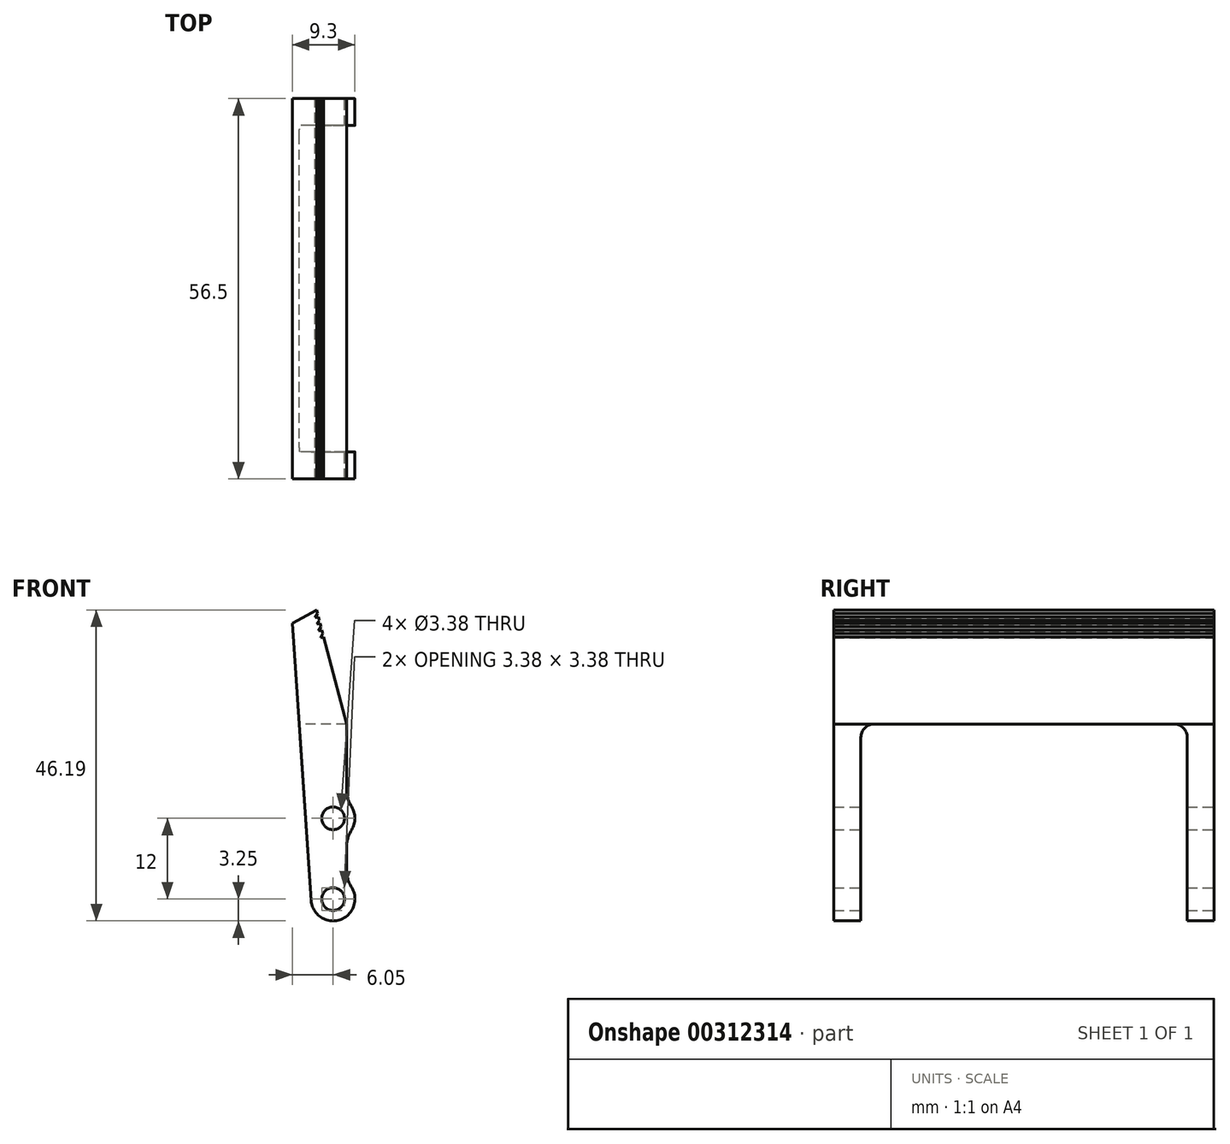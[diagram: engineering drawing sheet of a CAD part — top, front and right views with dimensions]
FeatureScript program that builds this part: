
annotation { "Feature Type Name" : "Feature", "Feature Type Description" : "" }
export const myFeature = defineFeature(function(context is Context, id is Id, definition is map)
    precondition{}
    {
        {
            var Q0;
            Q0=qCreatedBy(makeId("Front.planeOp"),FACE);
            var sketch = newSketch(context, id + "F0", { "sketchPlane" : qUnion([Q0])});
            skCircle(sketch, "E0", {"center": v(0, 0) * mm, "radius": 1.69 * mm});
            skCircle(sketch, "E1", {"center": v(0, 0) * mm, "radius": 2 * mm});
            skLineSegment(sketch, "E2", {"start": v(2, 16) * mm, "end": v(2, 14.56) * mm});
            skLineSegment(sketch, "E3", {"start": v(2, 26.01) * mm, "end": v(2, 16) * mm});
            skLineSegment(sketch, "E4", {"start": v(-6.05, 41) * mm, "end": v(-2, 0) * mm, "construction": true});
            skPoint(sketch, "E5.start.orphan", {"position": v(-6.03, 16) * mm});
            skPoint(sketch, "E6.center.orphan", {"position": v(0, 16) * mm});
            skCircle(sketch, "E7", {"center": v(0, 12) * mm, "radius": 1.69 * mm});
            skLineSegment(sketch, "E8", {"start": v(-6.05, 41) * mm, "end": v(-2.44, 42.94) * mm});
            skLineSegment(sketch, "E9", {"start": v(-2.44, 42.94) * mm, "end": v(2, 26.01) * mm});
            skLineSegment(sketch, "E10", {"start": v(2, 26.01) * mm, "end": v(-6.05, 41) * mm, "construction": true});
            skLineSegment(sketch, "E11", {"start": v(-2.66, 41.81) * mm, "end": v(-2.18, 41.94) * mm});
            skLineSegment(sketch, "E12", {"start": v(-2.31, 42.44) * mm, "end": v(-2.66, 41.81) * mm});
            skLineSegment(sketch, "E13", {"start": v(-2.05, 41.44) * mm, "end": v(-2.4, 40.81) * mm});
            skLineSegment(sketch, "E14", {"start": v(-2.4, 40.81) * mm, "end": v(-1.92, 40.94) * mm});
            skLineSegment(sketch, "E15", {"start": v(-1.79, 40.44) * mm, "end": v(-2.14, 39.81) * mm});
            skLineSegment(sketch, "E16", {"start": v(-2.14, 39.81) * mm, "end": v(-1.66, 39.94) * mm});
            skLineSegment(sketch, "E17", {"start": v(-1.52, 39.44) * mm, "end": v(-1.88, 38.81) * mm});
            skLineSegment(sketch, "E18", {"start": v(-1.88, 38.81) * mm, "end": v(-1.4, 38.94) * mm});
            skCircle(sketch, "E19", {"center": v(0, 0) * mm, "radius": 3.25 * mm});
            skArc(sketch, "E20", {"start": v(2, 9.44) * mm, "mid": v(3.25, 12) * mm, "end": v(2, 14.56) * mm});
            skLineSegment(sketch, "E21.trimOffspring", {"start": v(2, 9.44) * mm, "end": v(2, 0) * mm});
            skLineSegment(sketch, "E22", {"start": v(-3.24, -0.22) * mm, "end": v(-6.05, 41) * mm});
            skSolve(sketch);
        }
        {
            var Q0;
            Q0=makeQuery(id+"F0.imprint","IMPRINT",FACE,{"disambiguationData":[TD([[makeQuery(id+"F0.imprint","IMPRINT",EDGE,{"derivedFrom":sQuery(id+"F0.wireOp",EDGE,"E6")}),-1.0]])]});
            var Q1;
            Q1=makeQuery(id+"F0.imprint","IMPRINT",FACE,{"disambiguationData":[TD([[makeQuery(id+"F0.imprint","IMPRINT",EDGE,{"derivedFrom":sQuery(id+"F0.wireOp",EDGE,"E0")}),-1.0]])]});
            var Q2;
            {var subQ0=sQuery(id+"F0.wireOp",EDGE,"E2");Q2=makeQuery(id+"F0.imprint","IMPRINT",FACE,{"disambiguationData":[TD([[makeQuery(id+"F0.imprint","IMPRINT",EDGE,{"derivedFrom":subQ0}),-1.0]])]});}
            var Q3;
            {var subQ1=sQuery(id+"F0.wireOp",EDGE,"E3");Q3=makeQuery(id+"F0.imprint","IMPRINT",FACE,{"disambiguationData":[TD([[makeQuery(id+"F0.imprint","IMPRINT",EDGE,{"derivedFrom":subQ1}),-1.0]])]});}
            var Q4;
            {var subQ0=sQuery(id+"F0.wireOp",EDGE,"E2");var subQ1=sQuery(id+"F0.wireOp",EDGE,"E1");var subQ2=makeQuery(id+"F0.imprint","INTERSECT",VERTEX,{"derivedFrom":[subQ1,subQ0]});Q4=makeQuery(id+"F0.imprint","IMPRINT",FACE,{"disambiguationData":[TD([[makeQuery(id+"F0.imprint","IMPRINT",EDGE,{"disambiguationData":[TD([[subQ2,1.0]])],"derivedFrom":subQ1}),-1.0]])]});}
            extrude(context, id + "F1", {"entities" : qUnion([Q0, Q1, Q2, Q3, Q4]), "depth" : 56.5 * mm});
        }
        {
            var Q0;
            Q0=makeQuery(id+"F1.opExtrude","CAP_FACE",FACE,{"disambiguationData":[OSD([sQuery(id+"F0.wireOp",EDGE,"E0"),sQuery(id+"F0.wireOp",EDGE,"E1"),sQuery(id+"F0.wireOp",EDGE,"E2"),sQuery(id+"F0.wireOp",EDGE,"E3"),sQuery(id+"F0.wireOp",EDGE,"E4"),sQuery(id+"F0.wireOp",EDGE,"E7"),sQuery(id+"F0.wireOp",EDGE,"E8"),sQuery(id+"F0.wireOp",EDGE,"E9"),sQuery(id+"F0.wireOp",EDGE,"E11"),sQuery(id+"F0.wireOp",EDGE,"E12"),sQuery(id+"F0.wireOp",EDGE,"E13"),sQuery(id+"F0.wireOp",EDGE,"E14"),sQuery(id+"F0.wireOp",EDGE,"E15"),sQuery(id+"F0.wireOp",EDGE,"E16"),sQuery(id+"F0.wireOp",EDGE,"E17"),sQuery(id+"F0.wireOp",EDGE,"E18")])],"isStart":true});
            var sketch = newSketch(context, id + "F2", { "sketchPlane" : qUnion([Q0])});
            skLineSegment(sketch, "E23", {"start": v(-2, 26.01) * mm, "end": v(5.03, 26.01) * mm});
            skLineSegment(sketch, "E24", {"start": v(-2, 26.01) * mm, "end": v(-2.58, 13.98) * mm});
            skArc(sketch, "E25", {"start": v(-2.58, 13.98) * mm, "mid": v(-3.25, 12.16) * mm, "end": v(-2.76, 10.28) * mm});
            skLineSegment(sketch, "E26.trimOffspring", {"start": v(-2.76, 10.28) * mm, "end": v(-3.25, 0.16) * mm});
            skArc(sketch, "E27", {"start": v(-3.25, 0.16) * mm, "mid": v(-0.19, -3.24) * mm, "end": v(3.24, -0.22) * mm});
            skLineSegment(sketch, "E28", {"start": v(5.03, 26.01) * mm, "end": v(3.24, -0.22) * mm});
            skSolve(sketch);
        }
        {
            var Q0;
            Q0 = qSketchRegion(id + "F2", true);
            extrude(context, id + "F3", {"entities" : qUnion([Q0]), "operationType" : NewBodyOperationType.REMOVE, "oppositeDirection" : true, "depth" : 52.5 * mm, "hasSecondDirection" : true, "secondDirectionOppositeDirection" : true, "secondDirectionDepth" : 4 * mm});
        }
        {
            var Q0;
            {var subQ0=sQuery(id+"F0.wireOp",EDGE,"E19");var subQ1=sQuery(id+"F0.wireOp",EDGE,"E7");var subQ2=sQuery(id+"F0.wireOp",EDGE,"E4");var subQ3=sQuery(id+"F0.wireOp",EDGE,"E3");var subQ4=sQuery(id+"F0.wireOp",EDGE,"E2");var subQ5=sQuery(id+"F0.wireOp",EDGE,"E0");Q0=makeQuery(id+"F3.boolean.opBoolean","SPLIT",EDGE,{"disambiguationData":[TD([makeQuery(id+"F3.opExtrude","CAP_FACE",FACE,{"disambiguationData":[OSD([subQ5,subQ4,subQ3,subQ2,subQ1,subQ0,sQuery(id+"F2.wireOp",EDGE,"E23"),sQuery(id+"F2.wireOp",EDGE,"xCrteuFZ-jKkX-qwOT-CXdW-AAW16tBn9MUb")])],"isStart":false})])],"derivedFrom":makeQuery(id+"F1.opExtrude","SWEPT_EDGE",EDGE,{"disambiguationData":[OSD([subQ4,subQ0])]})});}
            var Q1;
            {var subQ0=sQuery(id+"F0.wireOp",EDGE,"E19");var subQ1=sQuery(id+"F0.wireOp",EDGE,"E7");var subQ2=sQuery(id+"F0.wireOp",EDGE,"E4");var subQ3=sQuery(id+"F0.wireOp",EDGE,"E3");var subQ4=sQuery(id+"F0.wireOp",EDGE,"E2");var subQ5=sQuery(id+"F0.wireOp",EDGE,"E0");Q1=makeQuery(id+"F3.boolean.opBoolean","SPLIT",EDGE,{"disambiguationData":[TD([makeQuery(id+"F3.opExtrude","CAP_FACE",FACE,{"disambiguationData":[OSD([subQ5,subQ4,subQ3,subQ2,subQ1,subQ0,sQuery(id+"F2.wireOp",EDGE,"E23"),sQuery(id+"F2.wireOp",EDGE,"xCrteuFZ-jKkX-qwOT-CXdW-AAW16tBn9MUb")])],"isStart":false})])],"derivedFrom":makeQuery(id+"F1.opExtrude","SWEPT_EDGE",EDGE,{"disambiguationData":[OSD([subQ2,subQ0])]})});}
            var Q2;
            {var subQ0=sQuery(id+"F0.wireOp",EDGE,"E19");var subQ1=sQuery(id+"F0.wireOp",EDGE,"E7");var subQ2=sQuery(id+"F0.wireOp",EDGE,"E4");var subQ3=sQuery(id+"F0.wireOp",EDGE,"E3");var subQ4=sQuery(id+"F0.wireOp",EDGE,"E2");var subQ5=sQuery(id+"F0.wireOp",EDGE,"E0");Q2=makeQuery(id+"F3.boolean.opBoolean","SPLIT",EDGE,{"disambiguationData":[TD([makeQuery(id+"F3.opExtrude","CAP_FACE",FACE,{"disambiguationData":[OSD([subQ5,subQ4,subQ3,subQ2,subQ1,subQ0,sQuery(id+"F2.wireOp",EDGE,"E23"),sQuery(id+"F2.wireOp",EDGE,"xCrteuFZ-jKkX-qwOT-CXdW-AAW16tBn9MUb")])],"isStart":true})])],"derivedFrom":makeQuery(id+"F1.opExtrude","SWEPT_EDGE",EDGE,{"disambiguationData":[OSD([subQ4,subQ0])]})});}
            var Q3;
            {var subQ0=sQuery(id+"F0.wireOp",EDGE,"E19");var subQ1=sQuery(id+"F0.wireOp",EDGE,"E7");var subQ2=sQuery(id+"F0.wireOp",EDGE,"E4");var subQ3=sQuery(id+"F0.wireOp",EDGE,"E3");var subQ4=sQuery(id+"F0.wireOp",EDGE,"E2");var subQ5=sQuery(id+"F0.wireOp",EDGE,"E0");Q3=makeQuery(id+"F3.boolean.opBoolean","SPLIT",EDGE,{"disambiguationData":[TD([makeQuery(id+"F3.opExtrude","CAP_FACE",FACE,{"disambiguationData":[OSD([subQ5,subQ4,subQ3,subQ2,subQ1,subQ0,sQuery(id+"F2.wireOp",EDGE,"E23"),sQuery(id+"F2.wireOp",EDGE,"xCrteuFZ-jKkX-qwOT-CXdW-AAW16tBn9MUb")])],"isStart":true})])],"derivedFrom":makeQuery(id+"F1.opExtrude","SWEPT_EDGE",EDGE,{"disambiguationData":[OSD([subQ2,subQ0])]})});}
            fillet(context, id + "F4", {"entities" : qUnion([Q0, Q1, Q2, Q3]), "radius" : 5 * mm, "tangentPropagation" : true, "allowEdgeOverflow" : false});
        }
        {
            var Q0;
            {var subQ0=sQuery(id+"F0.wireOp",EDGE,"E21.trimOffspring");var subQ1=sQuery(id+"F0.wireOp",EDGE,"E20");var subQ2=sQuery(id+"F0.wireOp",EDGE,"E19");var subQ3=sQuery(id+"F0.wireOp",EDGE,"E7");var subQ4=sQuery(id+"F0.wireOp",EDGE,"E4");var subQ5=sQuery(id+"F0.wireOp",EDGE,"E3");var subQ6=sQuery(id+"F0.wireOp",EDGE,"E2");var subQ7=sQuery(id+"F0.wireOp",EDGE,"E0");Q0=makeQuery(id+"F3.boolean.opBoolean","SPLIT",EDGE,{"disambiguationData":[TD([makeQuery(id+"F3.opExtrude","CAP_FACE",FACE,{"disambiguationData":[OSD([subQ7,subQ6,subQ5,subQ4,subQ3,subQ2,subQ1,subQ0,sQuery(id+"F2.wireOp",EDGE,"E23"),sQuery(id+"F2.wireOp",EDGE,"xCrteuFZ-jKkX-qwOT-CXdW-AAW16tBn9MUb")])],"isStart":true})])],"derivedFrom":makeQuery(id+"F1.opExtrude","SWEPT_EDGE",EDGE,{"disambiguationData":[OSD([subQ1,subQ0])]})});}
            var Q1;
            {var subQ0=sQuery(id+"F0.wireOp",EDGE,"E21.trimOffspring");var subQ1=sQuery(id+"F0.wireOp",EDGE,"E20");var subQ2=sQuery(id+"F0.wireOp",EDGE,"E19");var subQ3=sQuery(id+"F0.wireOp",EDGE,"E7");var subQ4=sQuery(id+"F0.wireOp",EDGE,"E4");var subQ5=sQuery(id+"F0.wireOp",EDGE,"E3");var subQ6=sQuery(id+"F0.wireOp",EDGE,"E2");var subQ7=sQuery(id+"F0.wireOp",EDGE,"E0");Q1=makeQuery(id+"F3.boolean.opBoolean","SPLIT",EDGE,{"disambiguationData":[TD([makeQuery(id+"F3.opExtrude","CAP_FACE",FACE,{"disambiguationData":[OSD([subQ7,subQ6,subQ5,subQ4,subQ3,subQ2,subQ1,subQ0,sQuery(id+"F2.wireOp",EDGE,"E23"),sQuery(id+"F2.wireOp",EDGE,"xCrteuFZ-jKkX-qwOT-CXdW-AAW16tBn9MUb")])],"isStart":false})])],"derivedFrom":makeQuery(id+"F1.opExtrude","SWEPT_EDGE",EDGE,{"disambiguationData":[OSD([subQ1,subQ0])]})});}
            fillet(context, id + "F5", {"entities" : qUnion([Q0, Q1]), "radius" : 5 * mm, "tangentPropagation" : true, "allowEdgeOverflow" : false});
        }
        {
            var Q0;
            Q0=makeQuery(id+"F3.boolean.opBoolean","COPY",EDGE,{"derivedFrom":makeQuery(id+"F3.opExtrude","CAP_EDGE",EDGE,{"disambiguationData":[OSD([sQuery(id+"F2.wireOp",EDGE,"E23")])],"isStart":false})});
            var Q1;
            Q1=makeQuery(id+"F3.boolean.opBoolean","COPY",EDGE,{"derivedFrom":makeQuery(id+"F3.opExtrude","CAP_EDGE",EDGE,{"disambiguationData":[OSD([sQuery(id+"F2.wireOp",EDGE,"E23")])],"isStart":true})});
            fillet(context, id + "F6", {"entities" : qUnion([Q0, Q1]), "radius" : 2 * mm, "tangentPropagation" : true, "allowEdgeOverflow" : false});
        }
    });
